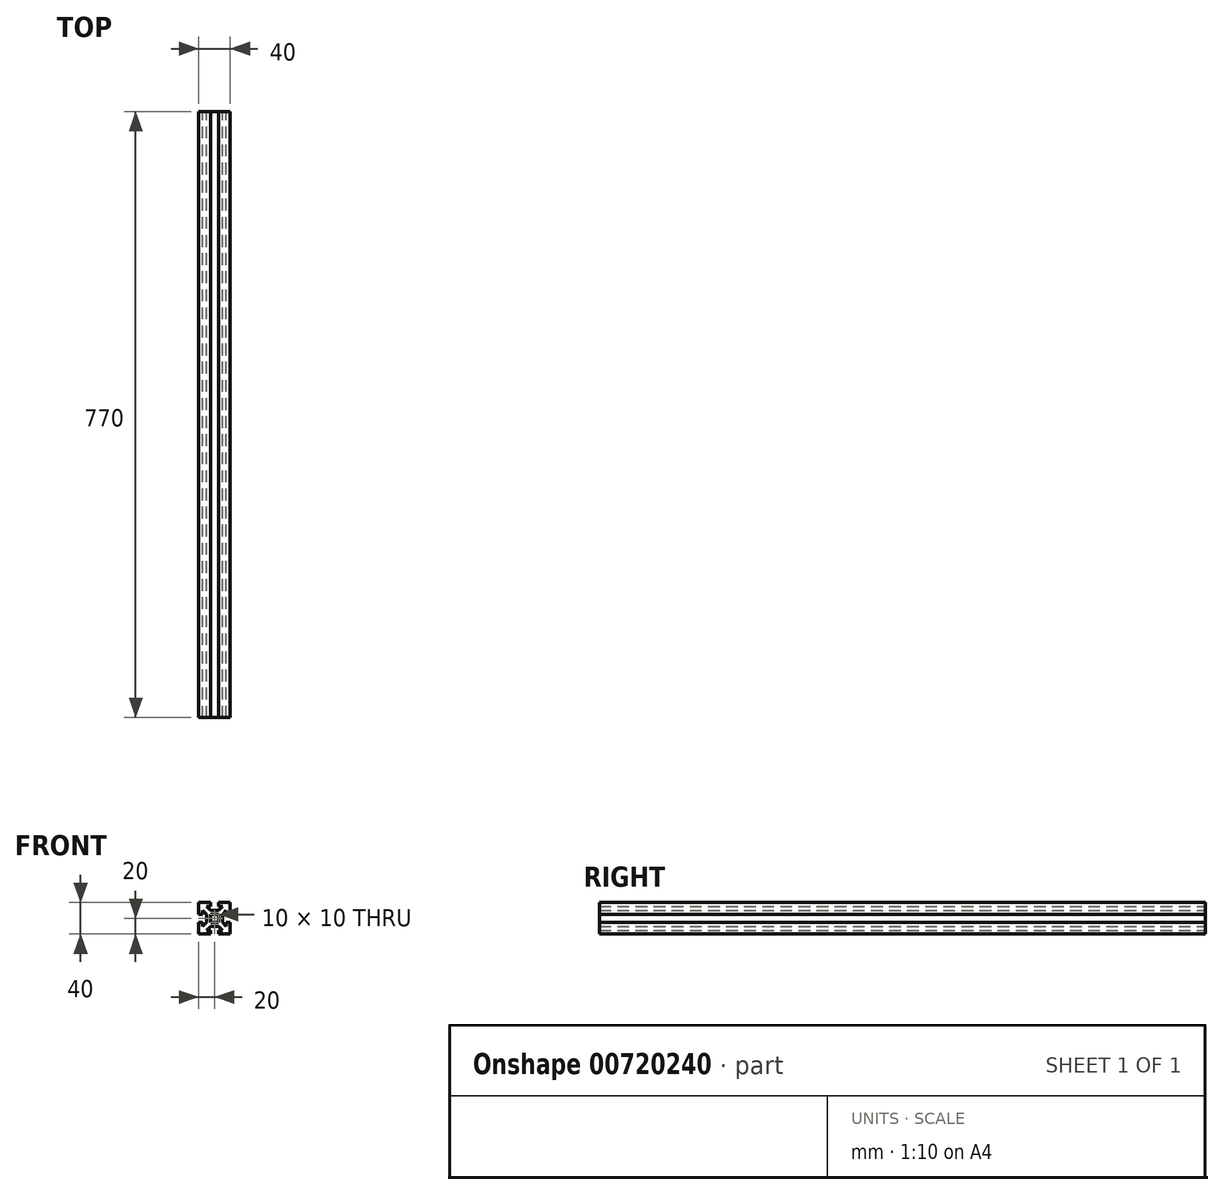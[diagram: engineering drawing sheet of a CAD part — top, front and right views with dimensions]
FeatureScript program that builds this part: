
annotation { "Feature Type Name" : "Feature", "Feature Type Description" : "" }
export const myFeature = defineFeature(function(context is Context, id is Id, definition is map)
    precondition{}
    {
        {
            var Q0;
            Q0=qCreatedBy(makeId("Front.planeOp"),FACE);
            var sketch = newSketch(context, id + "F0", { "sketchPlane" : qUnion([Q0])});
            skLineSegment(sketch, "E0.bottom", {"start": v(20, 20) * mm, "end": v(5, 20) * mm});
            skLineSegment(sketch, "E0.top", {"start": v(20, -20) * mm, "end": v(5, -20) * mm});
            skLineSegment(sketch, "E0.left", {"start": v(20, 20) * mm, "end": v(20, 5) * mm});
            skLineSegment(sketch, "E0.right", {"start": v(-20, 20) * mm, "end": v(-20, 5) * mm});
            skPoint(sketch, "E0.middle", {"position": v(0, 0) * mm});
            skLineSegment(sketch, "E1", {"start": v(0, 20) * mm, "end": v(0, -20) * mm, "construction": true});
            skLineSegment(sketch, "E2", {"start": v(-20, 0) * mm, "end": v(20, 0) * mm, "construction": true});
            skLineSegment(sketch, "E3", {"start": v(-20, 5) * mm, "end": v(-15, 5) * mm});
            skLineSegment(sketch, "E4", {"start": v(-20, -5) * mm, "end": v(-15, -5) * mm});
            skLineSegment(sketch, "E5", {"start": v(-5, 20) * mm, "end": v(-5, 15) * mm});
            skLineSegment(sketch, "E6", {"start": v(5, 20) * mm, "end": v(5, 15) * mm});
            skLineSegment(sketch, "E7", {"start": v(-10, 15) * mm, "end": v(-5, 15) * mm});
            skLineSegment(sketch, "E8", {"start": v(-10, -15) * mm, "end": v(-5, -15) * mm});
            skLineSegment(sketch, "E9", {"start": v(15, 10) * mm, "end": v(15, 5) * mm});
            skLineSegment(sketch, "E10", {"start": v(-15, 10) * mm, "end": v(-10, 5) * mm});
            skLineSegment(sketch, "E11", {"start": v(-10, 15) * mm, "end": v(-5, 10) * mm});
            skLineSegment(sketch, "E12", {"start": v(-15, -10) * mm, "end": v(-10, -5) * mm});
            skLineSegment(sketch, "E13", {"start": v(-10, -15) * mm, "end": v(-5, -10) * mm});
            skLineSegment(sketch, "E14.trimOffspring", {"start": v(20, -5) * mm, "end": v(20, -20) * mm});
            skLineSegment(sketch, "E15.trimOffspring", {"start": v(-20, -5) * mm, "end": v(-20, -20) * mm});
            skLineSegment(sketch, "E16.trimOffspring", {"start": v(-5, -20) * mm, "end": v(-20, -20) * mm});
            skLineSegment(sketch, "E17.trimOffspring", {"start": v(-5, 20) * mm, "end": v(-20, 20) * mm});
            skLineSegment(sketch, "E18.trimOffspring", {"start": v(5, 15) * mm, "end": v(10, 15) * mm});
            skLineSegment(sketch, "E19.trimOffspring", {"start": v(-15, -5) * mm, "end": v(-15, -10) * mm});
            skLineSegment(sketch, "E20.trimOffspring", {"start": v(15, -5) * mm, "end": v(15, -10) * mm});
            skLineSegment(sketch, "E21.trimOffspring", {"start": v(5, -15) * mm, "end": v(10, -15) * mm});
            skLineSegment(sketch, "E22.trimOffspring", {"start": v(-5, 5) * mm, "end": v(-5, -5) * mm});
            skLineSegment(sketch, "E23.trimOffspring", {"start": v(5, 5) * mm, "end": v(5, -5) * mm});
            skLineSegment(sketch, "E24.trimOffspring", {"start": v(15, 5) * mm, "end": v(20, 5) * mm});
            skLineSegment(sketch, "E25.trimOffspring", {"start": v(15, -5) * mm, "end": v(20, -5) * mm});
            skLineSegment(sketch, "E26.trimOffspring", {"start": v(5, -15) * mm, "end": v(5, -20) * mm});
            skLineSegment(sketch, "E27.trimOffspring", {"start": v(-5, -15) * mm, "end": v(-5, -20) * mm});
            skLineSegment(sketch, "E28.trimOffspring", {"start": v(-5, -5) * mm, "end": v(5, -5) * mm});
            skLineSegment(sketch, "E29.trimOffspring", {"start": v(-5, 5) * mm, "end": v(5, 5) * mm});
            skLineSegment(sketch, "E30", {"start": v(10, 5) * mm, "end": v(10, -5) * mm});
            skLineSegment(sketch, "E31", {"start": v(-5, 10) * mm, "end": v(5, 10) * mm});
            skLineSegment(sketch, "E32", {"start": v(-10, 5) * mm, "end": v(-10, -5) * mm});
            skLineSegment(sketch, "E33", {"start": v(-5, -10) * mm, "end": v(5, -10) * mm});
            skLineSegment(sketch, "E34.trimOffspring", {"start": v(-15, 10) * mm, "end": v(-15, 5) * mm});
            skPoint(sketch, "E35.orphan", {"position": v(20, 15) * mm});
            skPoint(sketch, "E36.orphan", {"position": v(20, -15) * mm});
            skPoint(sketch, "E37.orphan", {"position": v(15, -20) * mm});
            skPoint(sketch, "E38.orphan", {"position": v(-15, -20) * mm});
            skLineSegment(sketch, "E39.trimOffspring", {"start": v(-5, 0) * mm, "end": v(0, -5) * mm});
            skLineSegment(sketch, "E40.trimOffspring", {"start": v(-5, 0) * mm, "end": v(0, 5) * mm});
            skLineSegment(sketch, "E41.trimOffspring", {"start": v(0, 5) * mm, "end": v(5, 0) * mm});
            skLineSegment(sketch, "E42.trimOffspring", {"start": v(5, 10) * mm, "end": v(10, 15) * mm});
            skLineSegment(sketch, "E43.trimOffspring", {"start": v(10, 5) * mm, "end": v(15, 10) * mm});
            skLineSegment(sketch, "E44.trimOffspring", {"start": v(10, -5) * mm, "end": v(15, -10) * mm});
            skLineSegment(sketch, "E45.trimOffspring", {"start": v(5, -10) * mm, "end": v(10, -15) * mm});
            skLineSegment(sketch, "E46.trimOffspring", {"start": v(0, -5) * mm, "end": v(5, 0) * mm});
            skSolve(sketch);
        }
        {
            var Q0;
            Q0=makeQuery(id+"F0.imprint","IMPRINT",FACE,{"disambiguationData":[TD([[makeQuery(id+"F0.imprint","IMPRINT",EDGE,{"derivedFrom":sQuery(id+"F0.wireOp",EDGE,"E0.bottom")}),1.0]])]});
            extrude(context, id + "F1", {"entities" : qUnion([Q0]), "depth" : 770 * mm, "offsetDistance" : 25 * mm});
        }
    });
